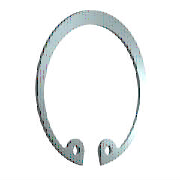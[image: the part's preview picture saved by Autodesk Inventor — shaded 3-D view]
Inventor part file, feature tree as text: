
AUTODESK INVENTOR PART (.ipt)
format: ipt  version: 2023.2 (Build 272271030, 271C)  size: 163,328 bytes
history: native  units: mm (DEFAULTED — no unit token found)
features: sketch x4, plane x3, other x2, hole x2
ambient origin geometry x8: Origin, YZ Plane, XZ Plane, XY Plane, X Axis, Y Axis, Z Axis, Center Point
bodies: Solid1 (feature_tree)
feature tree (11):
  plane  "WorkPlane1"
  plane  "Work Plane2"
  plane  "WorkPlane2"
  sketch  "Sketch1"  dims[d0=-2.0mm d1=5.2mm]
  other  "WorkPoint1"
  other  "WorkAxis1"
  hole  "Hole1"  [1 undecoded]
  hole  "Hole2"  [1 undecoded]
  sketch  "Sketch2"  dims[d2=29.2mm d3=0.0mm]
  sketch  "Sketch3"  dims[d4=0.0mm]
  sketch  "Sketch4"  dims[d5=4.227778mm d6=26.322222mm d7=0.283333mm d8=1.366667mm d9=3.12mm d10=6.5mm d11=3.12mm d12=6.5mm d13=1.08mm d14=2.25mm d15=1.08mm d16=2.25mm d17=3.66mm d18=25.65mm d19=3.66mm d20=25.65mm d21=6.283185mm d22=6.283185mm d23=6.283185mm d24=6.283185mm d25=2.0mm d26=0.0mm d27=0.0mm d28=0.0mm d29=2.5mm d30=6.0mm d31=4.0mm d32=2.0mm d33=60.0deg d34=8.0mm d35=20.594885mm d36=2.5mm d37=6.0mm d38=4.0mm d39=2.0mm d40=60.0deg d41=8.0mm d42=20.594885mm d47=0.0mm d48=0.0mm d49=0.0mm d50=0.0mm]
note: 2 required parameter values undecoded (feature->parameter linkage not recoverable at this tier; creation-order binding heuristic only, values carry confidence <= 0.55)
